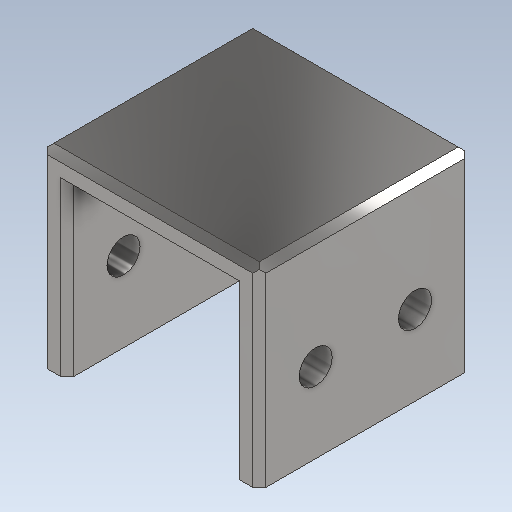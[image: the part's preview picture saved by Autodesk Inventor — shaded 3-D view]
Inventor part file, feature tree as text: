
AUTODESK INVENTOR PART (.ipt)
format: ipt  version: 2021 (Build 250183000, 183)  size: 224,256 bytes
history: native  units: mm
features: sketch x4, extrude x3, chamfer x2, hole x1, fillet x1, other x1
ambient origin geometry x8: Origin, YZ Plane, XZ Plane, XY Plane, X Axis, Y Axis, Z Axis, Center Point
bodies: Solid1 (feature_tree)
feature tree (12):
  extrude  "clamp_base"  Depth=66.0mm
  extrude  "clamp_extrusion"  TaperAngle=0.0deg  [1 undecoded]
  extrude  "platform"  Depth=50.0mm
  hole  "clampHole"  [1 undecoded]
  fillet  "Fillet1"  [1 undecoded]
  chamfer  "Chamfer1"  Distance=1149.0mm
  chamfer  "Chamfer2"  Distance=15.0mm
  other  "weld"
  sketch  "Sketch1"  dims[d0=58.0mm d1=66.0mm]
  sketch  "Sketch2"  dims[d2=33.0mm d3=0.0mm]
  sketch  "Sketch4"  dims[d4=64.0mm d5=0.0mm d6=50.0mm]
  sketch  "Sketch8"  dims[d7=50.0mm d8=25.0mm d9=0.0mm d10=0.0mm d12=1149.0mm d13=15.0mm d14=0.0mm d15=51.0mm d35=0.0mm d36=0.0mm d37=0.0mm d38=0.0mm d51=17.0mm d53=10.0mm d54=6.0mm d55=4.0mm d56=2.0mm d57=90.0deg d58=8.0mm d59=20.594885mm d60=30.0mm d61=64.0mm d81=2.0mm d82=2.0mm d83=2.0mm d84=45.0deg d90=2.0mm d91=2.0mm d92=45.0deg d94=6.981317mm d95=50.0mm d96=10.0mm d97=10.0mm]
note: 3 required parameter values undecoded (feature->parameter linkage not recoverable at this tier; creation-order binding heuristic only, values carry confidence <= 0.55)
